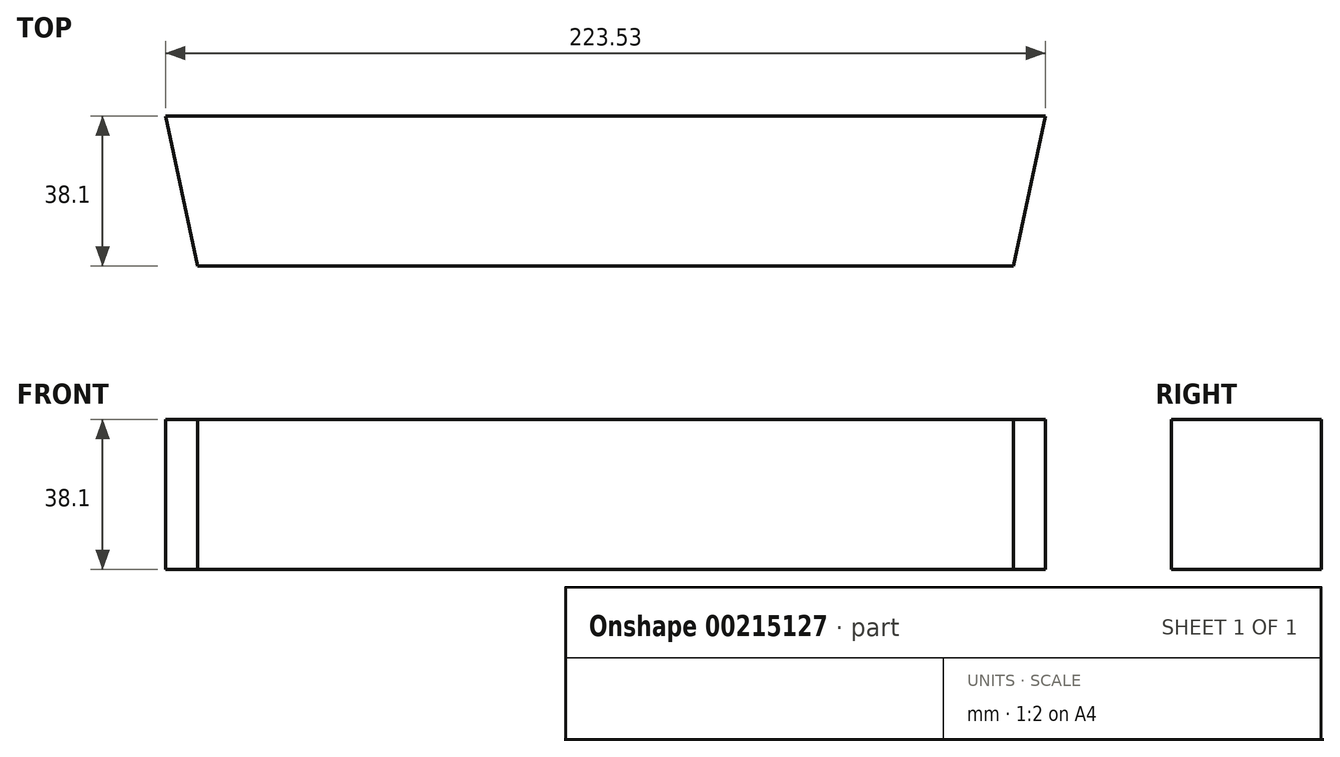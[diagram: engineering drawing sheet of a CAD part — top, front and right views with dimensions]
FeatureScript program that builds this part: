
annotation { "Feature Type Name" : "Feature", "Feature Type Description" : "" }
export const myFeature = defineFeature(function(context is Context, id is Id, definition is map)
    precondition{}
    {
        {
            var Q0;
            Q0=qCreatedBy(makeId("Top.planeOp"),FACE);
            var sketch = newSketch(context, id + "F0", { "sketchPlane" : qUnion([Q0])});
            skLineSegment(sketch, "E0", {"start": v(0, 0) * mm, "end": v(207.33, 0) * mm});
            skLineSegment(sketch, "E1", {"start": v(207.33, 0) * mm, "end": v(215.43, 38.1) * mm});
            skLineSegment(sketch, "E2", {"start": v(215.43, 38.1) * mm, "end": v(-8.1, 38.1) * mm});
            skLineSegment(sketch, "E3", {"start": v(-8.1, 38.1) * mm, "end": v(0, 0) * mm});
            skSolve(sketch);
        }
        {
            var Q0;
            Q0=makeQuery(id+"F0.imprint","IMPRINT",FACE,{"disambiguationData":[TD([[makeQuery(id+"F0.imprint","IMPRINT",EDGE,{"derivedFrom":sQuery(id+"F0.wireOp",EDGE,"E0")}),1.0]])]});
            extrude(context, id + "F1", {"entities" : qUnion([Q0]), "depth" : 38.1 * mm, "offsetDistance" : 25.4 * mm});
        }
    });
